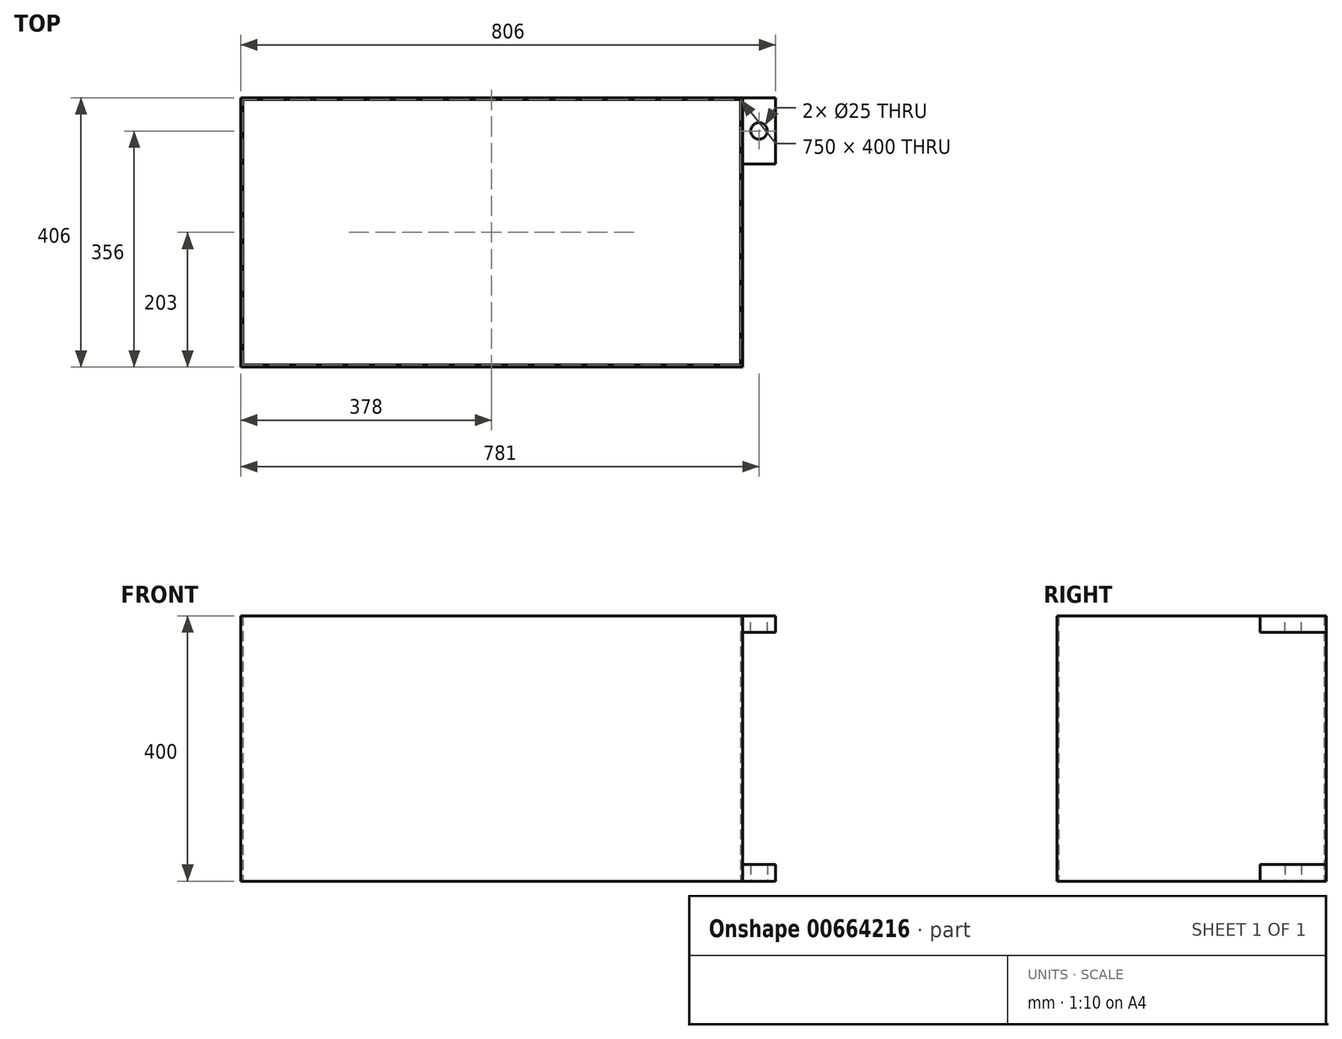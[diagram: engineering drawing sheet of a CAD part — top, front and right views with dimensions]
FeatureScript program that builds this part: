
annotation { "Feature Type Name" : "Feature", "Feature Type Description" : "" }
export const myFeature = defineFeature(function(context is Context, id is Id, definition is map)
    precondition{}
    {
        {
            var Q0;
            Q0=qCreatedBy(makeId("Top.planeOp"),FACE);
            var sketch = newSketch(context, id + "F0", { "sketchPlane" : qUnion([Q0])});
            skLineSegment(sketch, "E0.bottom", {"start": v(375, -200) * mm, "end": v(-375, -200) * mm});
            skLineSegment(sketch, "E0.top", {"start": v(375, 200) * mm, "end": v(-375, 200) * mm});
            skLineSegment(sketch, "E0.left", {"start": v(375, -200) * mm, "end": v(375, 200) * mm});
            skLineSegment(sketch, "E0.right", {"start": v(-375, -200) * mm, "end": v(-375, 200) * mm});
            skPoint(sketch, "E0.middle", {"position": v(0, 0) * mm});
            skLineSegment(sketch, "E1.0", {"start": v(378, 203) * mm, "end": v(-378, 203) * mm});
            skLineSegment(sketch, "E1.1", {"start": v(378, -203) * mm, "end": v(378, 203) * mm});
            skLineSegment(sketch, "E1.2", {"start": v(378, -203) * mm, "end": v(-378, -203) * mm});
            skLineSegment(sketch, "E1.3", {"start": v(-378, -203) * mm, "end": v(-378, 203) * mm});
            skSolve(sketch);
        }
        {
            var Q0;
            Q0=makeQuery(id+"F0.imprint","IMPRINT",FACE,{"disambiguationData":[TD([[makeQuery(id+"F0.imprint","IMPRINT",EDGE,{"derivedFrom":sQuery(id+"F0.wireOp",EDGE,"E0.bottom")}),1.0]])]});
            extrude(context, id + "F1", {"entities" : qUnion([Q0]), "depth" : 400 * mm, "offsetDistance" : 25 * mm});
        }
        {
            var Q0;
            Q0=makeQuery(id+"F1.opExtrude","SWEPT_FACE",FACE,{"disambiguationData":[OSD([sQuery(id+"F0.wireOp",EDGE,"E1.1")])]});
            var sketch = newSketch(context, id + "F2", { "sketchPlane" : qUnion([Q0])});
            skLineSegment(sketch, "E2.bottom", {"start": v(203, 400) * mm, "end": v(103, 400) * mm});
            skLineSegment(sketch, "E2.top", {"start": v(203, 375) * mm, "end": v(103, 375) * mm});
            skLineSegment(sketch, "E2.left", {"start": v(203, 400) * mm, "end": v(203, 375) * mm});
            skLineSegment(sketch, "E2.right", {"start": v(103, 400) * mm, "end": v(103, 375) * mm});
            skSolve(sketch);
        }
        {
            var Q0;
            Q0=makeQuery(id+"F2.imprint","IMPRINT",FACE,{"disambiguationData":[TD([[makeQuery(id+"F2.imprint","IMPRINT",EDGE,{"derivedFrom":sQuery(id+"F2.wireOp",EDGE,"E2.bottom")}),-1.0]])]});
            extrude(context, id + "F3", {"entities" : qUnion([Q0]), "depth" : 50 * mm, "offsetDistance" : 25 * mm});
        }
        {
            var Q0;
            Q0=makeQuery(id+"F3.opExtrude","SWEPT_FACE",FACE,{"disambiguationData":[OSD([sQuery(id+"F2.wireOp",EDGE,"E2.bottom")])]});
            var sketch = newSketch(context, id + "F4", { "sketchPlane" : qUnion([Q0])});
            skCircle(sketch, "E3", {"center": v(403, 153) * mm, "radius": 12.5 * mm});
            skPoint(sketch, "E3.centerSnap0", {"position": v(403, 203) * mm});
            skPoint(sketch, "E3.centerSnap1", {"position": v(378, 153) * mm});
            skSolve(sketch);
        }
        {
            var Q0;
            Q0=makeQuery(id+"F4.imprint","IMPRINT",FACE,{"disambiguationData":[TD([[makeQuery(id+"F4.imprint","IMPRINT",EDGE,{"derivedFrom":sQuery(id+"F4.wireOp",EDGE,"E3")}),1.0]])]});
            extrude(context, id + "F5", {"entities" : qUnion([Q0]), "operationType" : NewBodyOperationType.REMOVE, "oppositeDirection" : true, "depth" : 25 * mm, "offsetDistance" : 25 * mm});
        }
        {
            var Q0;
            Q0=qCreatedBy(makeId("Top.planeOp"),FACE);
            cPlane(context, id + "F6", {"entities" : qUnion([Q0]), "cplaneType" : CPlaneType.OFFSET, "offset" : 200 * mm, "width" : 150 * mm, "height" : 150 * mm});
        }
        {
            var Q0;
            Q0=makeQuery(id+"F3.opExtrude","SWEPT_BODY",BODY,{"disambiguationData":[OSD([sQuery(id+"F2.wireOp",EDGE,"E2.bottom"),sQuery(id+"F2.wireOp",EDGE,"E2.top"),sQuery(id+"F2.wireOp",EDGE,"E2.left"),sQuery(id+"F2.wireOp",EDGE,"E2.right")])]});
            var Q1;
            Q1=qCreatedBy(id+"F6.planeOp",FACE);
            mirror(context, id + "F7", {"entities" : qUnion([Q0]), "mirrorPlane" : qUnion([Q1])});
        }
    });
